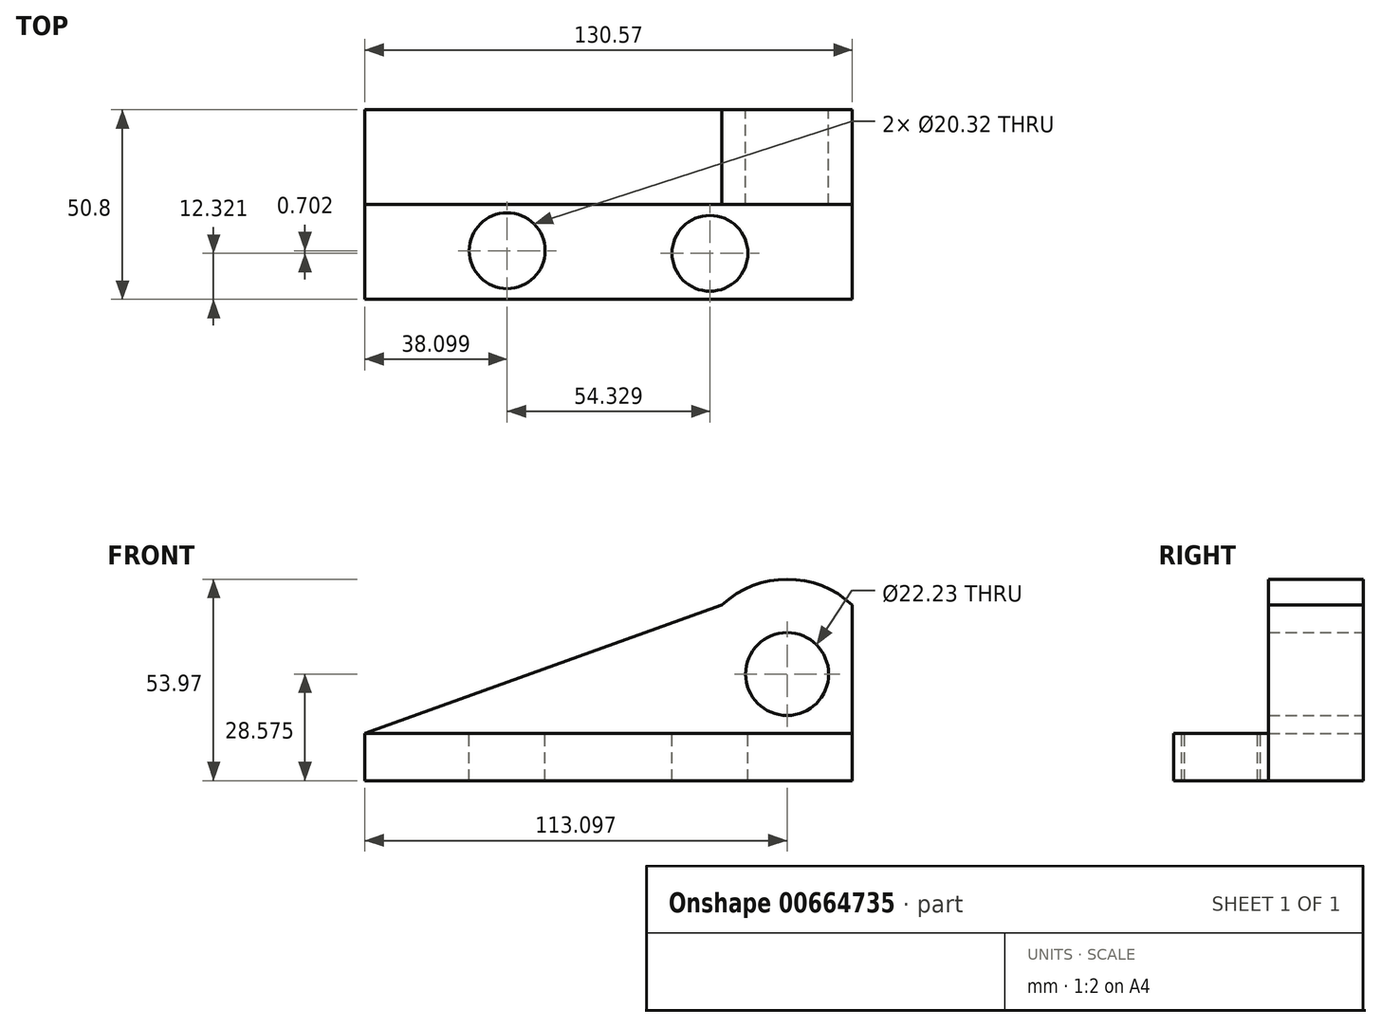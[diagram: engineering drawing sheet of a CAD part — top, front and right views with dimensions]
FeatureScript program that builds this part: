
annotation { "Feature Type Name" : "Feature", "Feature Type Description" : "" }
export const myFeature = defineFeature(function(context is Context, id is Id, definition is map)
    precondition{}
    {
        {
            var Q0;
            Q0=qCreatedBy(makeId("Front.planeOp"),FACE);
            var sketch = newSketch(context, id + "F0", { "sketchPlane" : qUnion([Q0])});
            skLineSegment(sketch, "E0", {"start": v(-63.12, 0) * mm, "end": v(-63.12, 12.7) * mm});
            skLineSegment(sketch, "E1", {"start": v(-63.12, 12.7) * mm, "end": v(32.5, 47.01) * mm});
            skArc(sketch, "E2", {"start": v(67.45, 47.01) * mm, "mid": v(49.98, 53.98) * mm, "end": v(32.5, 47.01) * mm});
            skLineSegment(sketch, "E3", {"start": v(67.45, 47.01) * mm, "end": v(67.45, 0) * mm});
            skLineSegment(sketch, "E4", {"start": v(-63.12, 0) * mm, "end": v(67.45, 0) * mm});
            skCircle(sketch, "E5", {"center": v(49.98, 28.58) * mm, "radius": 11.11 * mm});
            skLineSegment(sketch, "E6", {"start": v(49.98, 28.58) * mm, "end": v(49.98, 0) * mm});
            skSolve(sketch);
        }
        {
            var Q0;
            {var subQ1=sQuery(id+"F0.wireOp",EDGE,"E0");Q0=makeQuery(id+"F0.imprint","IMPRINT",FACE,{"disambiguationData":[TD([[makeQuery(id+"F0.imprint","IMPRINT",EDGE,{"derivedFrom":subQ1}),-1.0]])]});}
            extrude(context, id + "F1", {"entities" : qUnion([Q0]), "depth" : 25.4 * mm, "offsetDistance" : 25.4 * mm});
        }
        {
            var Q0;
            Q0=makeQuery(id+"F1.opExtrude","CAP_FACE",FACE,{"disambiguationData":[OSD([sQuery(id+"F0.wireOp",EDGE,"E0"),sQuery(id+"F0.wireOp",EDGE,"E1"),sQuery(id+"F0.wireOp",EDGE,"E2"),sQuery(id+"F0.wireOp",EDGE,"E3"),sQuery(id+"F0.wireOp",EDGE,"E4"),sQuery(id+"F0.wireOp",EDGE,"E5")])],"isStart":false});
            var sketch = newSketch(context, id + "F2", { "sketchPlane" : qUnion([Q0])});
            skSolve(sketch);
        }
        {
            var Q0;
            Q0=makeQuery(id+"F2.imprint","IMPRINT",FACE,{"disambiguationData":[TD([[makeQuery(id+"F2.imprint","IMPRINT",EDGE,{"derivedFrom":makeQuery(id+"F1.opExtrude","CAP_EDGE",EDGE,{"disambiguationData":[OSD([sQuery(id+"F0.wireOp",EDGE,"E0")])],"isStart":false})}),-1.0]])]});
            var sketch = newSketch(context, id + "F3", { "sketchPlane" : qUnion([Q0])});
            skLineSegment(sketch, "E7.bottom", {"start": v(-63.15, 12.7) * mm, "end": v(67.4, 12.7) * mm});
            skLineSegment(sketch, "E7.top", {"start": v(-63.15, 0) * mm, "end": v(67.4, 0) * mm});
            skLineSegment(sketch, "E7.left", {"start": v(-63.15, 12.7) * mm, "end": v(-63.15, 0) * mm});
            skLineSegment(sketch, "E7.right", {"start": v(67.4, 12.7) * mm, "end": v(67.4, 0) * mm});
            skSolve(sketch);
        }
        {
            var Q0;
            {var subQ0=sQuery(id+"F3.wireOp",EDGE,"E7.right");Q0=makeQuery(id+"F3.imprint","IMPRINT",FACE,{"disambiguationData":[TD([[makeQuery(id+"F3.imprint","IMPRINT",EDGE,{"derivedFrom":subQ0}),-1.0]])]});}
            extrude(context, id + "F4", {"entities" : qUnion([Q0]), "operationType" : NewBodyOperationType.ADD, "depth" : 25.4 * mm, "offsetDistance" : 25.4 * mm});
        }
        {
            var Q0;
            Q0=makeQuery(id+"F4.opExtrude","SWEPT_FACE",FACE,{"disambiguationData":[OSD([sQuery(id+"F3.wireOp",EDGE,"E7.bottom")])]});
            var sketch = newSketch(context, id + "F5", { "sketchPlane" : qUnion([Q0])});
            skPoint(sketch, "E8", {"position": v(-25.02, -37.78) * mm});
            skPoint(sketch, "E9", {"position": v(29.3, -38.48) * mm});
            skSolve(sketch);
        }
        {
            var Q0;
            Q0=sQuery(id+"F5.wireOp",VERTEX,"E8");
            var Q1;
            Q1=sQuery(id+"F5.wireOp",VERTEX,"E9");
            var Q2;
            Q2=makeQuery(id+"F1.opExtrude","SWEPT_BODY",BODY,{"disambiguationData":[OSD([sQuery(id+"F0.wireOp",EDGE,"E0"),sQuery(id+"F0.wireOp",EDGE,"E1"),sQuery(id+"F0.wireOp",EDGE,"E2"),sQuery(id+"F0.wireOp",EDGE,"E3"),sQuery(id+"F0.wireOp",EDGE,"E4"),sQuery(id+"F0.wireOp",EDGE,"E5")])]});
            hole(context, id + "F6", {"style" : HoleStyle.SIMPLE, "endStyle" : HoleEndStyle.THROUGH, "holeDiameter" : 20.32 * mm, "majorDiameter" : 6.35 * mm, "isTappedThrough" : true, "tappedDepth" : 12.7 * mm, "tapClearance" : 3, "locations" : qUnion([Q0, Q1]), "scope" : qUnion([Q2])});
        }
    });
